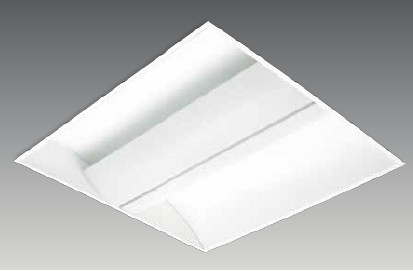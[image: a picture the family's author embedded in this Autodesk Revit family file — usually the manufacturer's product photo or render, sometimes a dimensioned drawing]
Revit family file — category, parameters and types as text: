
# Revit family: G 6060 EPB
name_source: partatom
category: Lighting Fixtures
revit_build: Autodesk Revit 2017 (Build: 20160225_1515(x64)
units: mm (PartAtom-declared; Revit-internal decimal feet)

## family parameters
Always vertical = Yes
Cut with Voids When Loaded = No
Host = Ceiling
Light Source = Yes
OmniClass Number = 23.80.70.11
OmniClass Title = Luminaries for Internal Lighting
Part Type = Normal
Room Calculation Point = No
Round Connector Dimension = Use Diameter
Shared = No

## types (2) — shared parameters
Color Filter = 16777215
Dimming Lamp Color Temperature Shift = <None>
Emit Shape Visible in Rendering = No
Emit from Rectangle Length = 570 mm  [stored 1.87008 ft]
Emit from Rectangle Width = 570 mm  [stored 1.87008 ft]
Light Source Symbol Size = 610 mm
Manufacturer = ARLIGHT
Type Image = G 6060 EPB.PNG
Wattage Comments = 44W

## type names (no varying parameters)
- GEPB.6060.44.30
- GEPB.6060.44.40

note: [stored X ft] marks values corroborated as IEEE doubles in the binary element streams (Revit-internal decimal feet)

## geometry (parser evidence)
native form markers: Sweep x2
no freeform markers — native parametric forms only
